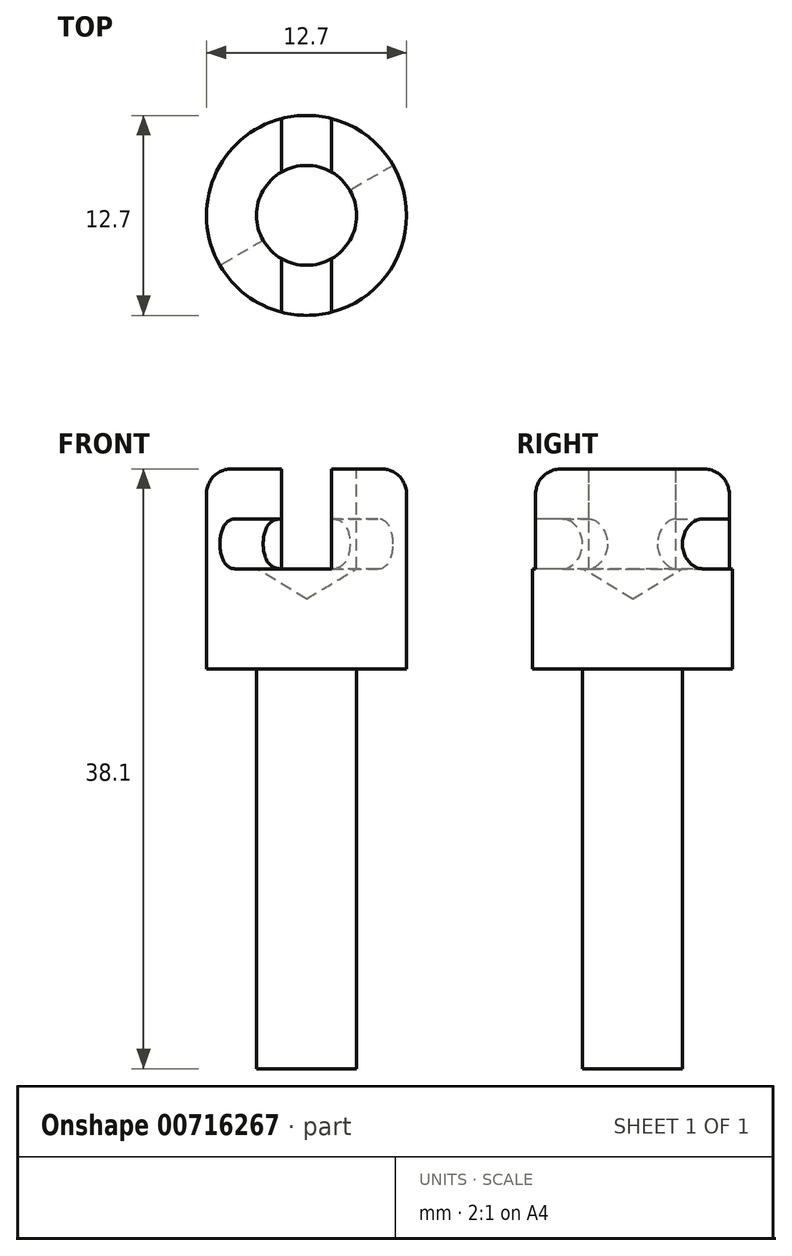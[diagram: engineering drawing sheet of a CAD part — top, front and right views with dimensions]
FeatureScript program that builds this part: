
annotation { "Feature Type Name" : "Feature", "Feature Type Description" : "" }
export const myFeature = defineFeature(function(context is Context, id is Id, definition is map)
    precondition{}
    {
        {
            var Q0;
            Q0=qCreatedBy(makeId("Top.planeOp"),FACE);
            var sketch = newSketch(context, id + "F0", { "sketchPlane" : qUnion([Q0])});
            skCircle(sketch, "E0", {"center": v(0, 0) * mm, "radius": 6.35 * mm});
            skSolve(sketch);
        }
        {
            var Q0;
            Q0=makeQuery(id+"F0.imprint","IMPRINT",FACE,{"disambiguationData":[TD([[makeQuery(id+"F0.imprint","IMPRINT",EDGE,{"derivedFrom":sQuery(id+"F0.wireOp",EDGE,"LVv9ohBu-0Fig-xdkc-Trhl-Ko3iAdXcgtPr")}),1.0]])]});
            var Q1;
            Q1=makeQuery(id+"F0.imprint","IMPRINT",FACE,{"disambiguationData":[TD([[makeQuery(id+"F0.imprint","IMPRINT",EDGE,{"derivedFrom":sQuery(id+"F0.wireOp",EDGE,"E0")}),1.0]])]});
            extrude(context, id + "F1", {"entities" : qUnion([Q0, Q1]), "depth" : 12.7 * mm, "offsetDistance" : 25.4 * mm});
        }
        {
            var Q0;
            Q0=qCreatedBy(makeId("Top.planeOp"),FACE);
            var sketch = newSketch(context, id + "F2", { "sketchPlane" : qUnion([Q0])});
            skCircle(sketch, "E1", {"center": v(0, 0) * mm, "radius": 3.18 * mm});
            skSolve(sketch);
        }
        {
            var Q0;
            Q0=makeQuery(id+"F2.imprint","IMPRINT",FACE,{"disambiguationData":[TD([[makeQuery(id+"F2.imprint","IMPRINT",EDGE,{"derivedFrom":sQuery(id+"F2.wireOp",EDGE,"E1")}),1.0]])]});
            var Q1;
            Q1=sQuery(id+"F2.wireOp",EDGE,"E1");
            extrude(context, id + "F3", {"entities" : qUnion([Q0]), "surfaceEntities" : qUnion([Q1]), "oppositeDirection" : true, "depth" : 25.4 * mm, "offsetDistance" : 25.4 * mm});
        }
        {
            var Q0;
            Q0=makeQuery(id+"F1.opExtrude","CAP_FACE",FACE,{"disambiguationData":[OSD([sQuery(id+"F0.wireOp",EDGE,"E0")])],"isStart":false});
            var sketch = newSketch(context, id + "F4", { "sketchPlane" : qUnion([Q0])});
            skCircle(sketch, "E2", {"center": v(0, 0) * mm, "radius": 3.18 * mm});
            skSolve(sketch);
        }
        {
            var Q0;
            Q0=sQuery(id+"F4.wireOp",VERTEX,"E2.center");
            var Q1;
            Q1=makeQuery(id+"F1.opExtrude","SWEPT_BODY",BODY,{"disambiguationData":[OSD([sQuery(id+"F0.wireOp",EDGE,"E0")])]});
            hole(context, id + "F5", {"style" : HoleStyle.SIMPLE, "endStyle" : HoleEndStyle.BLIND, "holeDiameter" : 6.35 * mm, "majorDiameter" : 6.35 * mm, "holeDepth" : 6.35 * mm, "isTappedThrough" : true, "tappedDepth" : 12.7 * mm, "tapClearance" : 3, "startFromSketch" : true, "locations" : qUnion([Q0]), "scope" : qUnion([Q1])});
        }
        {
            var Q0;
            Q0=makeQuery(id+"F1.opExtrude","CAP_FACE",FACE,{"disambiguationData":[OSD([sQuery(id+"F0.wireOp",EDGE,"E0")])],"isStart":false});
            var sketch = newSketch(context, id + "F6", { "sketchPlane" : qUnion([Q0])});
            skLineSegment(sketch, "E3.bottom", {"start": v(1.59, 6.35) * mm, "end": v(-1.59, 6.35) * mm});
            skLineSegment(sketch, "E3.top", {"start": v(1.59, -6.35) * mm, "end": v(-1.59, -6.35) * mm});
            skLineSegment(sketch, "E3.left", {"start": v(1.59, 6.35) * mm, "end": v(1.59, -6.35) * mm});
            skLineSegment(sketch, "E3.right", {"start": v(-1.59, 6.35) * mm, "end": v(-1.59, -6.35) * mm});
            skPoint(sketch, "E3.middle", {"position": v(0, 0) * mm});
            skSolve(sketch);
        }
        {
            var Q0;
            {var subQ0=makeQuery(id+"F1.opExtrude","CAP_EDGE",EDGE,{"disambiguationData":[OSD([sQuery(id+"F0.wireOp",EDGE,"E0")])],"isStart":false});var subQ1=makeQuery(id+"F6.imprint","INTERSECT",VERTEX,{"derivedFrom":[subQ0,sQuery(id+"F6.wireOp",EDGE,"E3.top")]});Q0=makeQuery(id+"F6.imprint","IMPRINT",FACE,{"disambiguationData":[TD([[makeQuery(id+"F6.imprint","IMPRINT",EDGE,{"disambiguationData":[TD([[subQ1,-1.0]])],"derivedFrom":subQ0}),1.0]])]});}
            var Q1;
            {var subQ0=makeQuery(id+"F1.opExtrude","CAP_EDGE",EDGE,{"disambiguationData":[OSD([sQuery(id+"F0.wireOp",EDGE,"E0")])],"isStart":false});var subQ1=makeQuery(id+"F6.imprint","INTERSECT",VERTEX,{"derivedFrom":[subQ0,sQuery(id+"F6.wireOp",EDGE,"E3.bottom")]});Q1=makeQuery(id+"F6.imprint","IMPRINT",FACE,{"disambiguationData":[TD([[makeQuery(id+"F6.imprint","IMPRINT",EDGE,{"disambiguationData":[TD([[subQ1,1.0]])],"derivedFrom":subQ0}),1.0]])]});}
            extrude(context, id + "F7", {"entities" : qUnion([Q0, Q1]), "operationType" : NewBodyOperationType.REMOVE, "oppositeDirection" : true, "depth" : 6.35 * mm, "offsetDistance" : 25.4 * mm});
        }
        {
            var Q0;
            Q0=qCreatedBy(makeId("Right.planeOp"),FACE);
            var sketch = newSketch(context, id + "F8", { "sketchPlane" : qUnion([Q0])});
            skLineSegment(sketch, "E4", {"start": v(0, 0) * mm, "end": v(0, 12.7) * mm});
            skSolve(sketch);
        }
        {
            var Q0;
            Q0=qCreatedBy(makeId("Right.planeOp"),FACE);
            var sketch = newSketch(context, id + "F9", { "sketchPlane" : qUnion([Q0])});
            skLineSegment(sketch, "E5.bottom", {"start": v(-6.35, 9.53) * mm, "end": v(6.35, 9.53) * mm});
            skLineSegment(sketch, "E5.top", {"start": v(-6.35, 6.35) * mm, "end": v(6.35, 6.35) * mm});
            skLineSegment(sketch, "E5.left", {"start": v(-6.35, 9.53) * mm, "end": v(-6.35, 6.35) * mm});
            skLineSegment(sketch, "E5.right", {"start": v(6.35, 9.53) * mm, "end": v(6.35, 6.35) * mm});
            skPoint(sketch, "E5.middle", {"position": v(0, 7.94) * mm});
            skSolve(sketch);
        }
        {
            var Q0;
            Q0=makeQuery(id+"F9.imprint","IMPRINT",FACE,{"disambiguationData":[TD([[makeQuery(id+"F9.imprint","IMPRINT",EDGE,{"derivedFrom":sQuery(id+"F9.wireOp",EDGE,"E5.bottom")}),-1.0]])]});
            var sketch = newSketch(context, id + "F10", { "sketchPlane" : qUnion([Q0])});
            skLineSegment(sketch, "E6.bottom", {"start": v(-6.35, 9.52) * mm, "end": v(-1.59, 9.52) * mm});
            skLineSegment(sketch, "E6.top", {"start": v(-6.35, 6.35) * mm, "end": v(-1.59, 6.35) * mm});
            skLineSegment(sketch, "E6.left", {"start": v(-6.35, 9.53) * mm, "end": v(-6.35, 6.35) * mm});
            skLineSegment(sketch, "E6.right", {"start": v(-1.59, 9.53) * mm, "end": v(-1.59, 6.35) * mm});
            skLineSegment(sketch, "E7.bottom", {"start": v(6.35, 6.35) * mm, "end": v(1.57, 6.35) * mm});
            skLineSegment(sketch, "E7.top", {"start": v(6.35, 9.53) * mm, "end": v(1.57, 9.53) * mm});
            skLineSegment(sketch, "E7.left", {"start": v(6.35, 6.35) * mm, "end": v(6.35, 9.53) * mm});
            skLineSegment(sketch, "E7.right", {"start": v(1.57, 6.35) * mm, "end": v(1.57, 9.53) * mm});
            skSolve(sketch);
        }
        {
            var Q0;
            Q0 = qSketchRegion(id + "F10", true);
            var Q1;
            Q1=sQuery(id+"F8.wireOp",EDGE,"E4");
            revolve(context, id + "F11", {"operationType" : NewBodyOperationType.REMOVE, "surfaceOperationType" : NewSurfaceOperationType.NEW, "entities" : qUnion([Q0]), "axis" : qUnion([Q1]), "revolveType" : RevolveType.ONE_DIRECTION, "oppositeDirection" : true, "angle" : 60 * degree});
        }
        {
            var Q0;
            Q0=makeQuery(id+"F11.boolean.opBoolean","COPY",EDGE,{"derivedFrom":makeQuery(id+"F11.opRevolve","CAP_EDGE",EDGE,{"disambiguationData":[OSD([sQuery(id+"F10.wireOp",EDGE,"E6.bottom")]),OD(0.0)],"isStart":false})});
            var Q1;
            Q1=makeQuery(id+"F11.boolean.opBoolean","COPY",EDGE,{"derivedFrom":makeQuery(id+"F11.opRevolve","CAP_EDGE",EDGE,{"disambiguationData":[OSD([sQuery(id+"F10.wireOp",EDGE,"E6.top")]),OD(0.0)],"isStart":false})});
            var Q2;
            Q2=makeQuery(id+"F11.boolean.opBoolean","COPY",EDGE,{"derivedFrom":makeQuery(id+"F11.opRevolve","CAP_EDGE",EDGE,{"disambiguationData":[OSD([sQuery(id+"F10.wireOp",EDGE,"E7.top")])],"isStart":false})});
            var Q3;
            Q3=makeQuery(id+"F11.boolean.opBoolean","COPY",EDGE,{"derivedFrom":makeQuery(id+"F11.opRevolve","CAP_EDGE",EDGE,{"disambiguationData":[OSD([sQuery(id+"F10.wireOp",EDGE,"E7.bottom")])],"isStart":false})});
            fillet(context, id + "F12", {"entities" : qUnion([Q0, Q1, Q2, Q3]), "radius" : 1.59 * mm, "tangentPropagation" : true, "allowEdgeOverflow" : false});
        }
        {
            var Q0;
            {var subQ0=sQuery(id+"F0.wireOp",EDGE,"E0");var subQ1=sQuery(id+"F6.wireOp",EDGE,"E3.right");var subQ2=makeQuery(id+"F1.opExtrude","CAP_EDGE",EDGE,{"disambiguationData":[OSD([subQ0])],"isStart":false});Q0=makeQuery(id+"F7.boolean.opBoolean","SPLIT",EDGE,{"disambiguationData":[TD([makeQuery(id+"F7.opExtrude","SWEPT_FACE",FACE,{"disambiguationData":[OSD([subQ1]),TDD([makeQuery(id+"F6.imprint","IMPRINT",EDGE,{"disambiguationData":[TD([[makeQuery(id+"F6.imprint","INTERSECT",VERTEX,{"disambiguationData":[OD(0.0)],"derivedFrom":[subQ2,subQ1]}),-1.0]])],"derivedFrom":subQ1})])]})])],"derivedFrom":subQ2});}
            var Q1;
            {var subQ0=sQuery(id+"F0.wireOp",EDGE,"E0");var subQ1=sQuery(id+"F6.wireOp",EDGE,"E3.left");var subQ2=makeQuery(id+"F1.opExtrude","CAP_EDGE",EDGE,{"disambiguationData":[OSD([subQ0])],"isStart":false});Q1=makeQuery(id+"F7.boolean.opBoolean","SPLIT",EDGE,{"disambiguationData":[TD([makeQuery(id+"F7.opExtrude","SWEPT_FACE",FACE,{"disambiguationData":[OSD([subQ1]),TDD([makeQuery(id+"F6.imprint","IMPRINT",EDGE,{"disambiguationData":[TD([[makeQuery(id+"F6.imprint","INTERSECT",VERTEX,{"disambiguationData":[OD(0.0)],"derivedFrom":[subQ2,subQ1]}),-1.0]])],"derivedFrom":subQ1})])]})])],"derivedFrom":subQ2});}
            fillet(context, id + "F13", {"entities" : qUnion([Q0, Q1]), "radius" : 1.59 * mm, "tangentPropagation" : true, "allowEdgeOverflow" : false});
        }
    });
